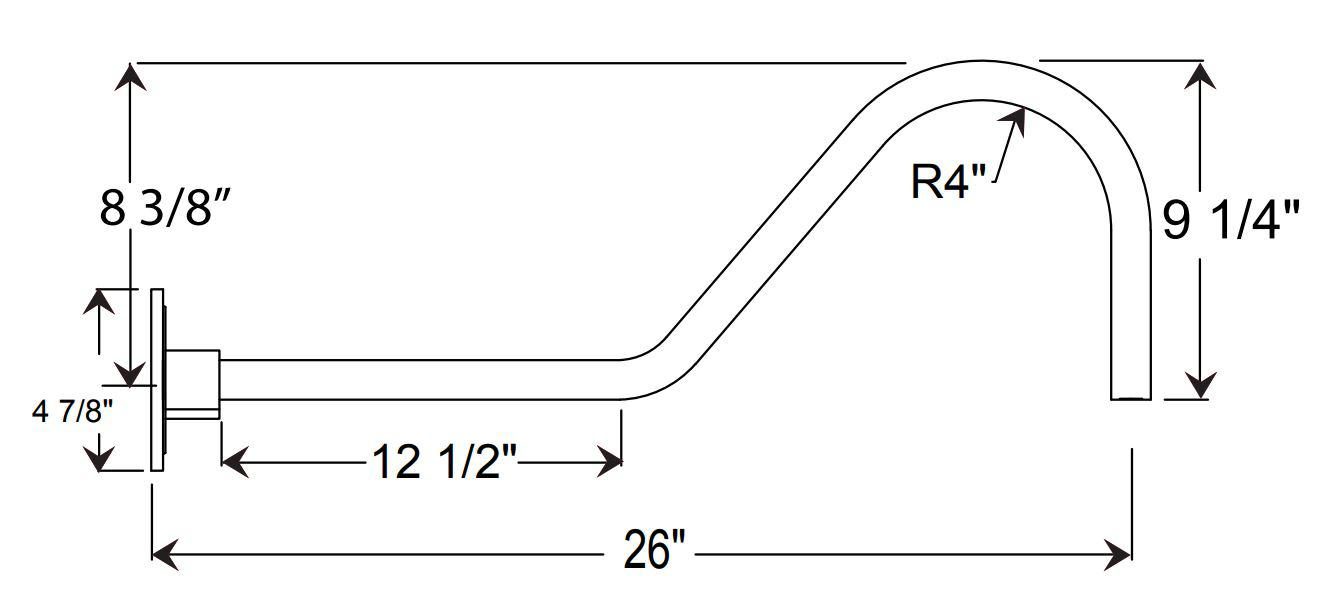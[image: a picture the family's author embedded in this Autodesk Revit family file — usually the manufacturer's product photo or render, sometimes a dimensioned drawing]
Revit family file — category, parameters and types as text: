
# Revit family: SPM- GUP111 MB
name_source: partatom
category: Lighting Fixtures
units: mm (PartAtom-declared; Revit-internal decimal feet)

## family parameters
Always vertical = Yes
Cut with Voids When Loaded = No
Light Source = Yes
OmniClass Number = 23.80.70.00
OmniClass Title = Lighting
Part Type = Normal
Room Calculation Point = No
Round Connector Dimension = Use Diameter
Shared = No
Work Plane-Based = No

## types (1)
- SPM-GUP111
    Apparent Load = 200 VA
    Body Colour = Spun aluminium
    Body Material = body
    Color Filter = 16777215
    Construction Material = Heavy Duty spun aluminum.
    Default Elevation = 0' - 0"
    Description = 120-277 Voltage
    Dimming Lamp Color Temperature Shift = <None>
    Fixture Diameter = 0' - 6 1/2"
    Fixture Height = 0' - 11"
    GLASS = Glass
    Lamp = MED-BASE
    Load Classification = Lighting
    Manufacturer = ANP Lighting
    Model = SPM-GUP111
    Photometric Web File = generic.ies
    Power Factor = 1
    Ring = RING
    SPM-GUP111 = Yes
    Tilt Angle = 90.00°
    URL = https://www.anplighting.com
    Voltage = 277 V
    Warranty = 5 year limited warranty
    Wattage Comments = 200W Max
    Weight = 1.5 lbs

## geometry (parser evidence)
native form markers: Sweep x20
no freeform markers — native parametric forms only
